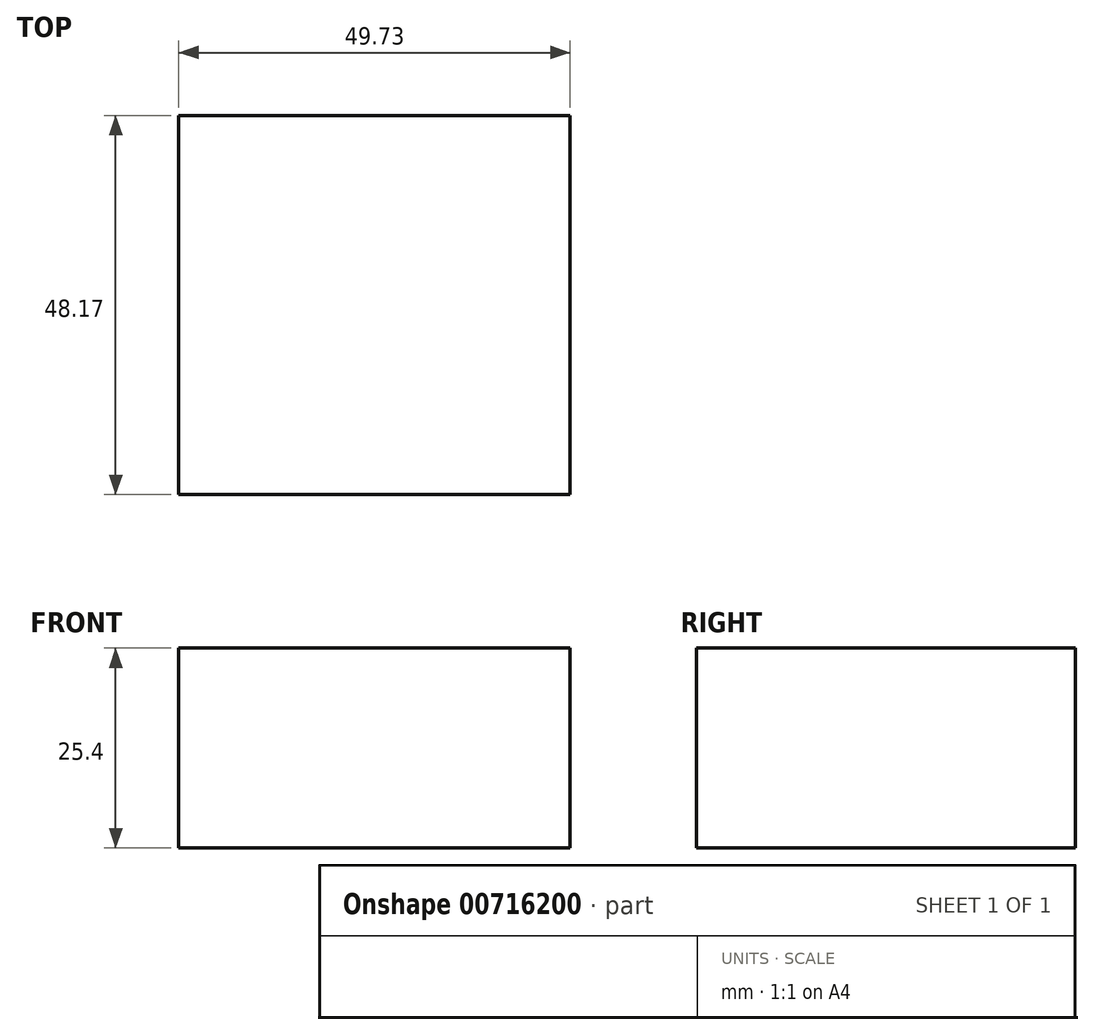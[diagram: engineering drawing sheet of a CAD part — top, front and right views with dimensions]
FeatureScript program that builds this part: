
annotation { "Feature Type Name" : "Feature", "Feature Type Description" : "" }
export const myFeature = defineFeature(function(context is Context, id is Id, definition is map)
    precondition{}
    {
        {
            var Q0;
            Q0=qCreatedBy(makeId("Top.planeOp"),FACE);
            var sketch = newSketch(context, id + "F0", { "sketchPlane" : qUnion([Q0])});
            skLineSegment(sketch, "E0.bottom", {"start": v(0, 0) * mm, "end": v(-49.73, 0) * mm});
            skLineSegment(sketch, "E0.top", {"start": v(0, -48.17) * mm, "end": v(-49.73, -48.17) * mm});
            skLineSegment(sketch, "E0.left", {"start": v(0, 0) * mm, "end": v(0, -48.17) * mm});
            skLineSegment(sketch, "E0.right", {"start": v(-49.73, 0) * mm, "end": v(-49.73, -48.17) * mm});
            skSolve(sketch);
        }
        {
            var Q0;
            Q0 = qSketchRegion(id + "F0", true);
            extrude(context, id + "F1", {"entities" : qUnion([Q0]), "depth" : 25.4 * mm, "offsetDistance" : 25.4 * mm});
        }
    });
